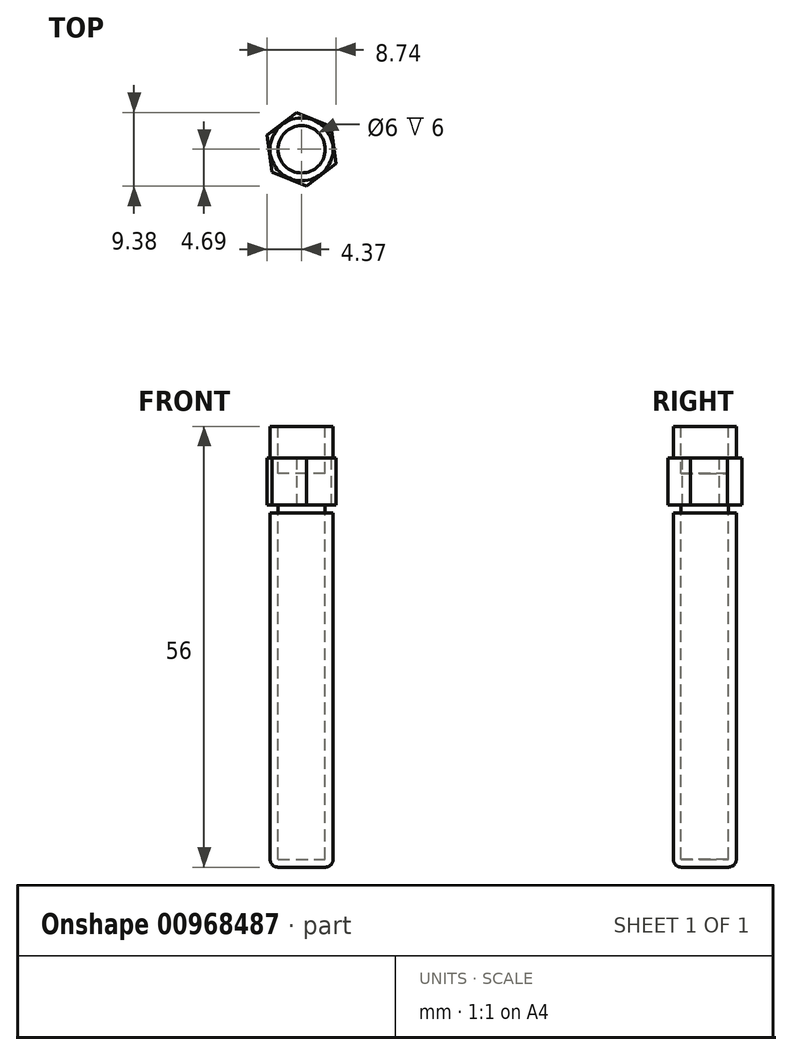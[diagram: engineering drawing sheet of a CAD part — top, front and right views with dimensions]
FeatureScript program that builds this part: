
annotation { "Feature Type Name" : "Feature", "Feature Type Description" : "" }
export const myFeature = defineFeature(function(context is Context, id is Id, definition is map)
    precondition{}
    {
        {
            var Q0;
            Q0=qCreatedBy(makeId("Top.planeOp"),FACE);
            var sketch = newSketch(context, id + "F0", { "sketchPlane" : qUnion([Q0])});
            skCircle(sketch, "E0.cCircle", {"center": v(0, 0) * mm, "radius": 4.1 * mm, "construction": true});
            skLineSegment(sketch, "E0.0", {"start": v(-0.62, 4.7) * mm, "end": v(3.75, 2.88) * mm});
            skLineSegment(sketch, "E0.1", {"start": v(3.75, 2.88) * mm, "end": v(4.37, -1.8) * mm});
            skLineSegment(sketch, "E0.2", {"start": v(4.37, -1.8) * mm, "end": v(0.62, -4.7) * mm});
            skLineSegment(sketch, "E0.3", {"start": v(0.62, -4.7) * mm, "end": v(-3.75, -2.88) * mm});
            skLineSegment(sketch, "E0.4", {"start": v(-3.75, -2.88) * mm, "end": v(-4.37, 1.8) * mm});
            skLineSegment(sketch, "E0.5", {"start": v(-4.37, 1.8) * mm, "end": v(-0.62, 4.7) * mm});
            skPoint(sketch, "E0.0.midPoint", {"position": v(1.57, 3.79) * mm});
            skSolve(sketch);
        }
        {
            var Q0;
            Q0 = qSketchRegion(id + "F0", true);
            extrude(context, id + "F1", {"entities" : qUnion([Q0]), "depth" : 6 * mm, "offsetDistance" : 25 * mm});
        }
        {
            var Q0;
            Q0=makeQuery(id+"F1.opExtrude","CAP_FACE",FACE,{"disambiguationData":[OSD([sQuery(id+"F0.wireOp",EDGE,"E0.0"),sQuery(id+"F0.wireOp",EDGE,"E0.1"),sQuery(id+"F0.wireOp",EDGE,"E0.2"),sQuery(id+"F0.wireOp",EDGE,"E0.3"),sQuery(id+"F0.wireOp",EDGE,"E0.4"),sQuery(id+"F0.wireOp",EDGE,"E0.5")])],"isStart":true});
            var sketch = newSketch(context, id + "F2", { "sketchPlane" : qUnion([Q0])});
            skCircle(sketch, "E1", {"center": v(0, 0) * mm, "radius": 3 * mm});
            skSolve(sketch);
        }
        {
            var Q0;
            Q0 = qSketchRegion(id + "F2", true);
            extrude(context, id + "F3", {"entities" : qUnion([Q0]), "operationType" : NewBodyOperationType.ADD, "depth" : 45 * mm, "offsetDistance" : 25 * mm});
        }
        {
            var Q0;
            Q0=makeQuery(id+"F1.opExtrude","CAP_FACE",FACE,{"disambiguationData":[OSD([sQuery(id+"F0.wireOp",EDGE,"E0.0"),sQuery(id+"F0.wireOp",EDGE,"E0.1"),sQuery(id+"F0.wireOp",EDGE,"E0.2"),sQuery(id+"F0.wireOp",EDGE,"E0.3"),sQuery(id+"F0.wireOp",EDGE,"E0.4"),sQuery(id+"F0.wireOp",EDGE,"E0.5")])],"isStart":false});
            var sketch = newSketch(context, id + "F4", { "sketchPlane" : qUnion([Q0])});
            skCircle(sketch, "E2", {"center": v(0, 0) * mm, "radius": 4 * mm});
            skSolve(sketch);
        }
        {
            var Q0;
            Q0 = qSketchRegion(id + "F4", true);
            extrude(context, id + "F5", {"entities" : qUnion([Q0]), "operationType" : NewBodyOperationType.ADD, "depth" : 4 * mm, "offsetDistance" : 25 * mm});
        }
        {
            var Q0;
            Q0=makeQuery(id+"F5.opExtrude","CAP_FACE",FACE,{"disambiguationData":[OSD([sQuery(id+"F4.wireOp",EDGE,"E2")])],"isStart":false});
            var sketch = newSketch(context, id + "F6", { "sketchPlane" : qUnion([Q0])});
            skCircle(sketch, "E3", {"center": v(0, 0) * mm, "radius": 3 * mm});
            skSolve(sketch);
        }
        {
            var Q0;
            Q0 = qSketchRegion(id + "F6", true);
            extrude(context, id + "F7", {"entities" : qUnion([Q0]), "operationType" : NewBodyOperationType.REMOVE, "oppositeDirection" : true, "depth" : 6 * mm, "offsetDistance" : 25 * mm});
        }
        {
            var Q0;
            Q0=qCreatedBy(makeId("Top.planeOp"),FACE);
            cPlane(context, id + "F8", {"entities" : qUnion([Q0]), "cplaneType" : CPlaneType.OFFSET, "offset" : 1 * mm, "oppositeDirection" : true, "width" : 150 * mm, "height" : 150 * mm});
        }
        {
            var Q0;
            Q0=qCreatedBy(id+"F8.planeOp",FACE);
            var sketch = newSketch(context, id + "F9", { "sketchPlane" : qUnion([Q0])});
            skCircle(sketch, "E4", {"center": v(0, 0) * mm, "radius": 4 * mm});
            skSolve(sketch);
        }
        {
            var Q0;
            Q0 = qSketchRegion(id + "F9", true);
            extrude(context, id + "F10", {"entities" : qUnion([Q0]), "oppositeDirection" : true, "depth" : 45 * mm, "offsetDistance" : 25 * mm});
        }
        {
            var Q0;
            Q0=makeQuery(id+"F10.opExtrude","CAP_EDGE",EDGE,{"disambiguationData":[OSD([sQuery(id+"F9.wireOp",EDGE,"E4")])],"isStart":false});
            fillet(context, id + "F11", {"entities" : qUnion([Q0]), "radius" : 1 * mm, "tangentPropagation" : true, "allowEdgeOverflow" : false});
        }
    });
